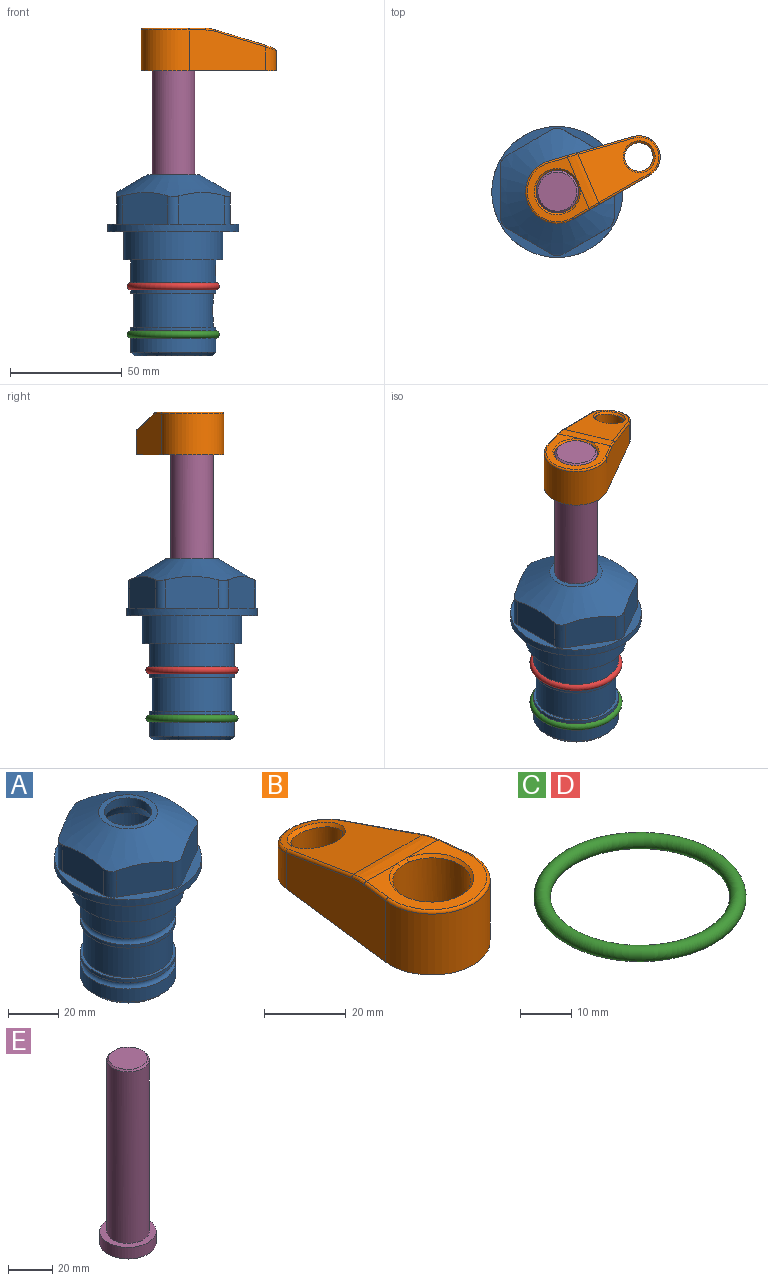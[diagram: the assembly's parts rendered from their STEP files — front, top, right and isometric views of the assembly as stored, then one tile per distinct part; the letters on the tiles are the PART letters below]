
ASSEMBLY  parts=5 mates=4
PART A: 36 faces, bbox 58.7x58.7x81 mm
  f0: cylinder r=17.78mm len=35.56mm, axis (0,0,1), area 1670.8mm2, adj f23,f24,f31
  f1: cylinder r=19.05mm len=38.1mm, axis (0,0,1), area 1191.9mm2, adj f26,f27,f30
  f2: plane 58.66x58.66mm, normal (0,0,-1), area 1150.6mm2, adj f3,f28
  f3: cylinder r=29.33mm len=58.66mm, axis (0,0,-1), area 585.1mm2, adj f2,f4
  f4: plane 58.66x58.66mm, normal (0,0,1), area 475.9mm2, adj f3,f5,f6,f7,f8,f9,f10,f11
  f5: plane 20.32x14.34mm, normal (-0.5,0.87,0), area 324.4mm2, adj f4,f15,f16,f17
  f6: plane 20.32x14.34mm, normal (0.5,0.87,0), area 324.4mm2, adj f4,f14,f15,f17
  f7: plane 23.48x14.34mm, normal (1,0,0), area 324.4mm2, adj f4,f13,f14,f17
  f8: plane 20.32x14.34mm, normal (0.5,-0.87,0), area 324.4mm2, adj f4,f12,f13,f17
  f9: plane 20.32x14.34mm, normal (-0.5,-0.87,0), area 324.4mm2, adj f4,f11,f12,f17
  f10: plane 23.48x14.34mm, normal (-1,0,0), area 324.4mm2, adj f4,f11,f16,f17
  f11: cylinder r=5.08mm len=12.85mm, axis (0,0,-1), area 67.2mm2, adj f4,f9,f10,f17
  f12: cylinder r=5.08mm len=12.85mm, axis (0,0,-1), area 67.2mm2, adj f4,f8,f9,f17
  f13: cylinder r=5.08mm len=12.85mm, axis (0,0,-1), area 67.2mm2, adj f4,f7,f8,f17
  f14: cylinder r=5.08mm len=12.85mm, axis (0,0,-1), area 67.2mm2, adj f4,f6,f7,f17
  f15: cylinder r=5.08mm len=12.85mm, axis (0,0,-1), area 67.2mm2, adj f4,f5,f6,f17
  f16: cylinder r=5.08mm len=12.85mm, axis (0,0,-1), area 67.2mm2, adj f4,f5,f10,f17
  f17: cone r=11.73mm half-angle=60deg, axis (0,0,-1), area 2071.8mm2, adj f5,f6,f7,f8,f9,f10,f11,f12
  f18: plane 23.46x23.46mm, normal (0,0,1), area 147.4mm2, adj f17,f35
  f19: plane 34.93x34.93mm, normal (0,0,-1), area 958mm2, adj f29
  f20: cylinder r=19.05mm len=38.1mm, axis (0,0,1), area 760.1mm2, adj f21,f29
  f21: torus R=19.05mm, axis (0,0,1), area 565.3mm2, adj f20,f22
  f22: cylinder r=19.05mm len=38.1mm, axis (0,0,1), area 190mm2, adj f21,f23
  f23: plane 38.1x38.1mm, normal (0,0,1), area 146.9mm2, adj f0,f22
  f24: plane 38.1x38.1mm, normal (0,0,-1), area 146.9mm2, adj f0,f25
  f25: cylinder r=19.05mm len=38.1mm, axis (0,0,1), area 190mm2, adj f24,f26
  f26: torus R=19.05mm, axis (0,0,1), area 565.3mm2, adj f1,f25
  f27: plane 44.45x44.45mm, normal (0,0,-1), area 411.7mm2, adj f1,f28
  f28: cylinder r=22.23mm len=44.45mm, axis (0,0,1), area 1773.5mm2, adj f2,f27
  f29: cone r=19.05mm half-angle=45deg, axis (0,0,1), area 257.5mm2, adj f19,f20
  f30: cylinder r=3.17mm len=6.75mm, axis (-1,0,0), area 128mm2, adj f1,f33
  f31: cylinder r=3.17mm len=6.35mm, axis (-1,0,0), area 102.5mm2, adj f0,f33
  f32: plane 25.4x25.4mm, normal (0,0,1), area 506.7mm2, adj f33
  f33: cylinder r=12.7mm len=66.42mm, axis (0,0,-1), area 5236.2mm2, adj f30,f31,f32,f34
  f34: cone r=9.53mm half-angle=30deg, axis (0,0,-1), area 443.4mm2, adj f33,f35
  f35: cylinder r=9.53mm len=19.05mm, axis (0,0,-1), area 240.9mm2, adj f18,f34
PART B: 31 faces, bbox 31.7x65.5x19.8 mm
  f0: plane 39.12x18.26mm, normal (0.99,0.12,0), area 612.2mm2, adj f1,f4,f7,f11,f13,f15
  f1: cylinder r=9.53mm len=18.91mm, axis (0,0,-1), area 296.1mm2, adj f0,f2,f7,f17
  f2: plane 39.12x18.26mm, normal (-0.99,0.12,0), area 612.2mm2, adj f1,f4,f7,f12,f14,f16
  f3: cylinder r=6.35mm len=12.7mm, axis (0,0,-1), area 362.4mm2, adj f7,f18
  f4: cylinder r=14.29mm len=28.58mm, axis (0,0,-1), area 882.2mm2, adj f0,f2,f7,f10
  f5: cylinder r=9.53mm len=19.05mm, axis (0,0,-1), area 1092.6mm2, adj f7,f19,f20
  f6: plane 26.99x23.69mm, normal (0,0,1), area 216.2mm2, adj f9,f10,f11,f12,f19
  f7: plane 63.5x28.58mm, normal (0,0,-1), area 661.8mm2, adj f0,f1,f2,f3,f4,f5,f22,f23
  f8: plane 33.52x23.6mm, normal (0,0.26,0.97), area 486mm2, adj f9,f15,f16,f17,f18
  f9: cylinder r=19.05mm len=24.72mm, axis (1,0,0), area 120.4mm2, adj f6,f8,f13,f14,f20
  f10: torus R=13.49mm, axis (0,0,1), area 59mm2, adj f4,f6,f11,f12
  f11: cylinder r=0.79mm len=8.67mm, axis (0.12,-0.99,0), area 10.8mm2, adj f0,f6,f10,f13
  f12: cylinder r=0.79mm len=8.67mm, axis (0.12,0.99,0), area 10.8mm2, adj f2,f6,f10,f14
  f13: bspline ~4.95x1.42mm, area 6.1mm2, adj f0,f9,f11,f15
  f14: bspline ~4.95x1.42mm, area 6.1mm2, adj f2,f9,f12,f16
  f15: cylinder r=0.79mm len=25.95mm, axis (0.12,-0.96,0.26), area 32.9mm2, adj f0,f8,f13,f17
  f16: cylinder r=0.79mm len=25.95mm, axis (0.12,0.96,-0.26), area 32.9mm2, adj f2,f8,f14,f17
  f17: bspline ~18.91x8.38mm, area 30mm2, adj f1,f8,f15,f16
  f18: bspline ~14.29x14.29mm, area 48.3mm2, adj f3,f8
  f19: cone r=9.53mm half-angle=45deg, axis (0,0,1), area 66.5mm2, adj f5,f6,f20
  f20: bspline ~3.22x0.96mm, area 3.5mm2, adj f5,f9,f19
  f21: plane 2.75x2.72mm, normal (0,0,-1), area 2.9mm2, adj f23,f25,f28
  f22: plane 23.05x15.88mm, normal (-0.99,-0.12,0), area 323.6mm2, adj f7,f25,f26,f27,f28,f29
  f23: plane 23.05x15.88mm, normal (0.99,-0.12,0), area 323.6mm2, adj f7,f21,f25,f27,f28,f30
  f24: cylinder r=9.53mm len=10.69mm, axis (0,0,-1), area 114.7mm2, adj f7,f27,f29,f30
  f25: cylinder r=12.7mm len=20.59mm, axis (0,0,-1), area 381.1mm2, adj f7,f21,f22,f23,f26,f28
  f26: plane 2.75x2.72mm, normal (0,0,-1), area 2.9mm2, adj f22,f25,f28
  f27: plane 19.72x18.37mm, normal (0,-0.26,-0.97), area 291.8mm2, adj f22,f23,f24,f28,f29,f30
  f28: cylinder r=15.88mm len=19.92mm, axis (1,0,0), area 54.8mm2, adj f21,f22,f23,f25,f26,f27
  f29: cylinder r=1.59mm len=11mm, axis (0,0,-1), area 34.7mm2, adj f7,f22,f24,f27
  f30: cylinder r=1.59mm len=11mm, axis (0,0,-1), area 34.7mm2, adj f7,f23,f24,f27
PART C: 1 faces, bbox 44.7x44.7x3.2 mm
  f0: torus R=19.05mm, axis (0,0,1), area 1193.9mm2
PART D: same geometry as C
PART E: 6 faces, bbox 25.4x25.4x101.6 mm
  f0: plane 17.46x17.46mm, normal (0,0,1), area 239.5mm2, adj f5
  f1: plane 25.4x25.4mm, normal (0,0,-1), area 506.7mm2, adj f2
  f2: cylinder r=12.7mm len=25.4mm, axis (0,0,1), area 506.7mm2, adj f1,f3
  f3: plane 25.4x25.4mm, normal (0,0,1), area 221.7mm2, adj f2,f4
  f4: cylinder r=9.53mm len=94.46mm, axis (0,0,1), area 5653mm2, adj f3,f5
  f5: cone r=8.73mm half-angle=45deg, axis (0,0,-1), area 64.4mm2, adj f0,f4
PLACE A at identity fixed
PLACE B rot(axis=(0,0,-1),67deg) t=(0,0,27.55)mm
PLACE C t=(0,0,-21.59)mm
PLACE D at identity
PLACE E rot(axis=(0,0,-1),67deg) t=(0,0,27.55)mm
MATE fastened E.f2 <-> B.f4  axis (0,0,1) through (0,0,91.05)mm
MATE cylindrical E.f2 <-> A.f0  axis (0,0,-1) through (0,0,-10.55)mm
MATE fastened C.f0 <-> A.f0  axis (0,0,1) through (0,0,-46.1)mm
MATE fastened D.f0 <-> A.f0  axis (0,0,1) through (0,0,-24.51)mm
